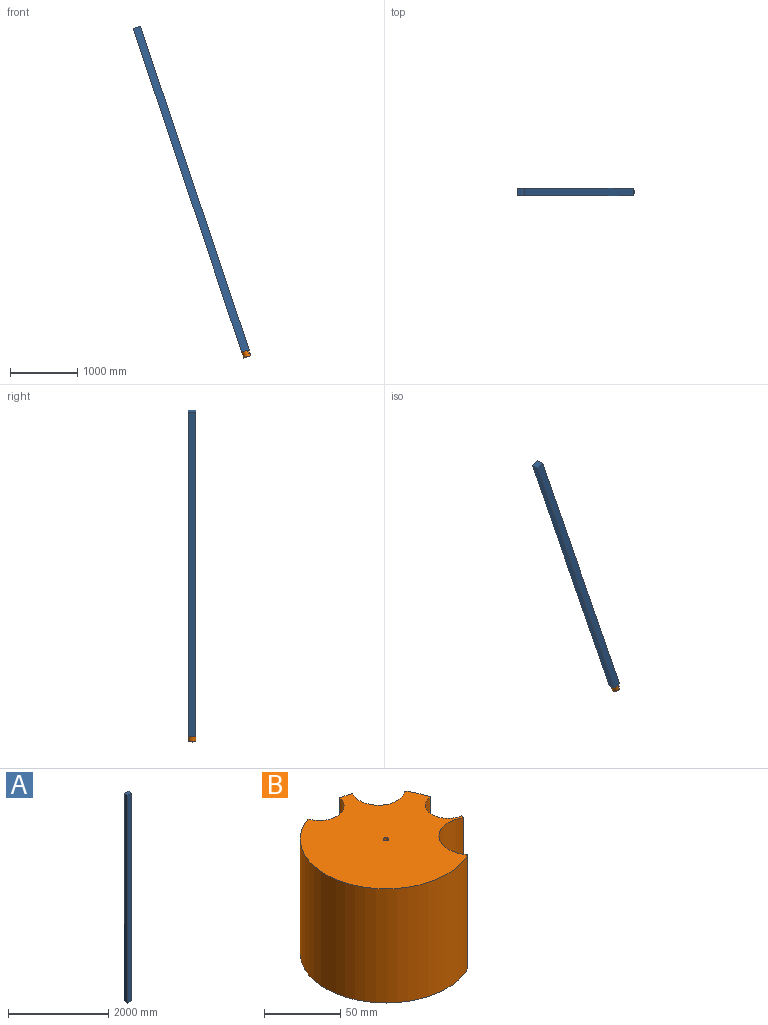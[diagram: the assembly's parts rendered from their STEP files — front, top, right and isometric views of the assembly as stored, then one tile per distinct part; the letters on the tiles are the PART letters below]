
ASSEMBLY  parts=2 mates=1
PART A: 6 faces, bbox 115x106.2x5080 mm
  f0: plane 5080x106.15mm, normal (1,0,0), area 539249.6mm2, adj f1,f3,f4,f5
  f1: plane 5080x115.02mm, normal (0,1,0), area 584315.6mm2, adj f0,f2,f4,f5
  f2: plane 5080x106.15mm, normal (-1,0,0), area 539249.6mm2, adj f1,f3,f4,f5
  f3: plane 5080x115.02mm, normal (0,-1,0), area 584315.6mm2, adj f0,f2,f4,f5
  f4: plane 115.02x106.15mm, normal (0,0,1), area 12209.8mm2, adj f0,f1,f2,f3
  f5: plane 115.02x106.15mm, normal (0,0,-1), area 12209.8mm2, adj f0,f1,f2,f3
PART B: 11 faces, bbox 110.9x111.3x91.7 mm
  f0: cylinder r=16.41mm len=91.68mm, axis (0,0,-1), area 3987.3mm2, adj f1,f7,f9,f10
  f1: cylinder r=56.26mm len=108.87mm, axis (0,0,-1), area 16754mm2, adj f0,f2,f9,f10
  f2: cylinder r=21.48mm len=91.68mm, axis (0,0,-1), area 5430.2mm2, adj f1,f3,f9,f10
  f3: cylinder r=56.26mm len=91.68mm, axis (0,0,-1), area 224.1mm2, adj f2,f4,f9,f10
  f4: cylinder r=14.97mm len=91.68mm, axis (0,0,-1), area 3945.6mm2, adj f3,f5,f9,f10
  f5: cylinder r=56.26mm len=91.68mm, axis (0,0,-1), area 1659.7mm2, adj f4,f6,f9,f10
  f6: cylinder r=17.31mm len=91.68mm, axis (0,0,-1), area 4496.1mm2, adj f5,f7,f9,f10
  f7: cylinder r=56.26mm len=91.68mm, axis (0,0,-1), area 908.9mm2, adj f0,f6,f9,f10
  f8: cylinder r=1.72mm len=91.68mm, axis (0,0,-1), area 989.9mm2, adj f9,f10
  f9: plane 111.28x110.86mm, normal (0,0,1), area 8155.1mm2, adj f0,f1,f2,f3,f4,f5,f6,f7
  f10: plane 111.28x110.86mm, normal (0,0,-1), area 8155.1mm2, adj f0,f1,f2,f3,f4,f5,f6,f7
PLACE A rot(axis=(0,-1,0),18.5deg) t=(55.81,126.23,57.05)mm
PLACE B rot(axis=(0,-1,0),18.5deg) t=(84.97,126.23,-29.87)mm
MATE fastened B.f1 <-> A.f5  axis (-0.32,0,0.95) through (55.81,126.23,57.05)mm
